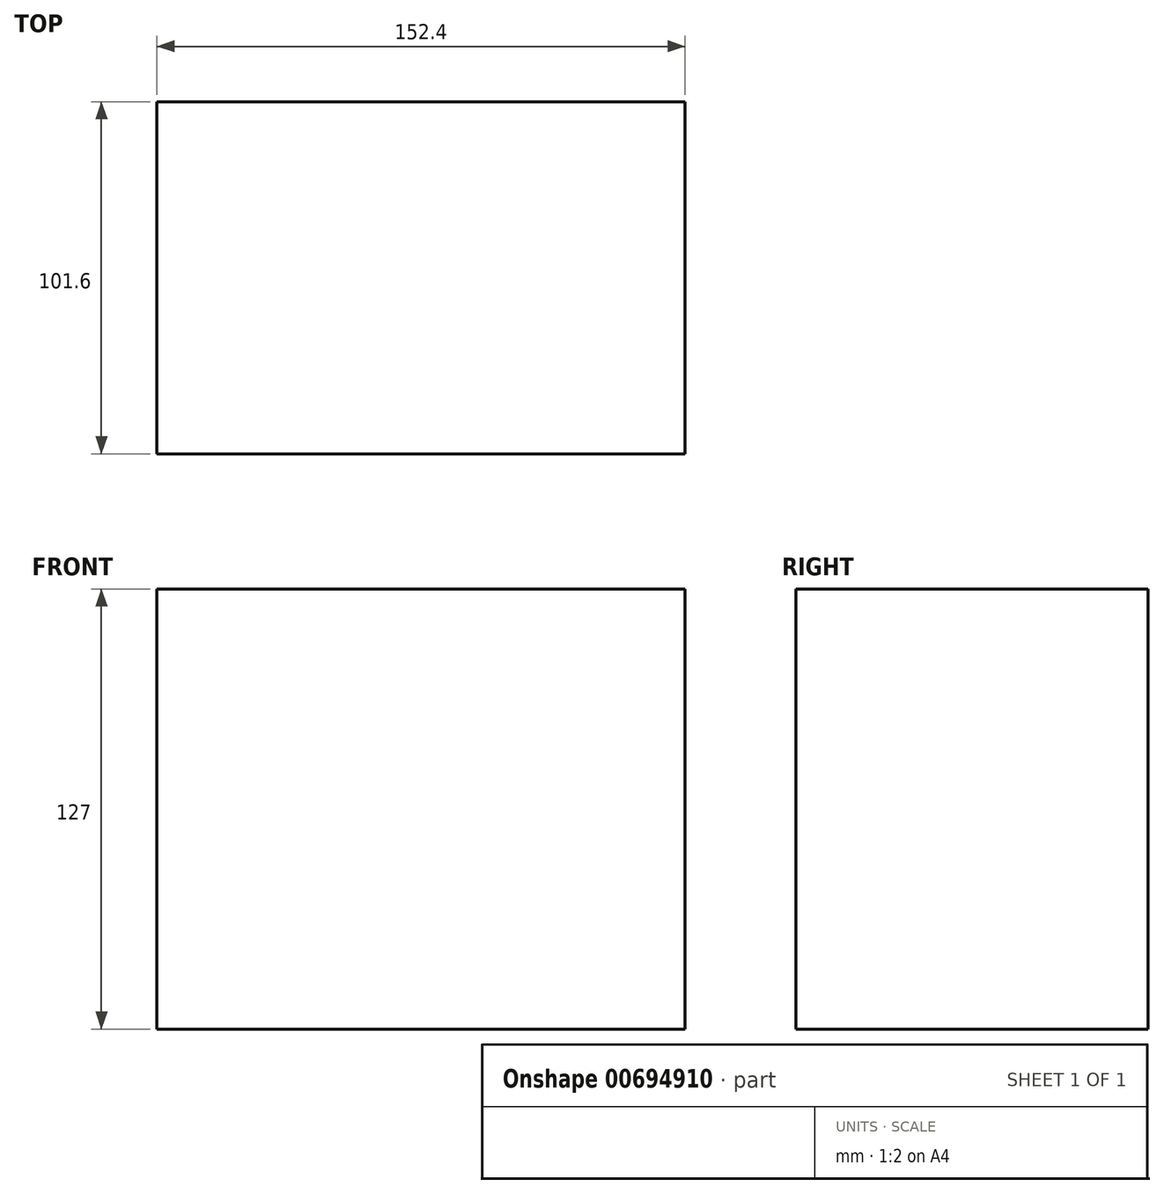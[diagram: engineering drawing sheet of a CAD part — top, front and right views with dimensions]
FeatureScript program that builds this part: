
annotation { "Feature Type Name" : "Feature", "Feature Type Description" : "" }
export const myFeature = defineFeature(function(context is Context, id is Id, definition is map)
    precondition{}
    {
        {
            var Q0;
            Q0=qCreatedBy(makeId("Front.planeOp"),FACE);
            var sketch = newSketch(context, id + "F0", { "sketchPlane" : qUnion([Q0])});
            skLineSegment(sketch, "E0.bottom", {"start": v(-103.49, 73.42) * mm, "end": v(48.91, 73.42) * mm});
            skLineSegment(sketch, "E0.top", {"start": v(-103.49, -28.18) * mm, "end": v(48.91, -28.18) * mm});
            skLineSegment(sketch, "E0.left", {"start": v(-103.49, 73.42) * mm, "end": v(-103.49, -28.18) * mm});
            skLineSegment(sketch, "E0.right", {"start": v(48.91, 73.42) * mm, "end": v(48.91, -28.18) * mm});
            skSolve(sketch);
        }
        {
            var Q0;
            Q0=makeQuery(id+"F0.imprint","IMPRINT",FACE,{"disambiguationData":[TD([[makeQuery(id+"F0.imprint","IMPRINT",EDGE,{"derivedFrom":sQuery(id+"F0.wireOp",EDGE,"E0.bottom")}),-1.0]])]});
            var sketch = newSketch(context, id + "F1", { "sketchPlane" : qUnion([Q0])});
            skLineSegment(sketch, "E1.bottom", {"start": v(-117.43, 108.75) * mm, "end": v(34.97, 108.75) * mm});
            skLineSegment(sketch, "E1.top", {"start": v(-117.43, -18.25) * mm, "end": v(34.97, -18.25) * mm});
            skLineSegment(sketch, "E1.left", {"start": v(-117.43, 108.75) * mm, "end": v(-117.43, -18.25) * mm});
            skLineSegment(sketch, "E1.right", {"start": v(34.97, 108.75) * mm, "end": v(34.97, -18.25) * mm});
            skSolve(sketch);
        }
        {
            var Q0;
            Q0 = qSketchRegion(id + "F1", true);
            extrude(context, id + "F2", {"entities" : qUnion([Q0]), "depth" : 101.6 * mm, "offsetDistance" : 25.4 * mm});
        }
    });
